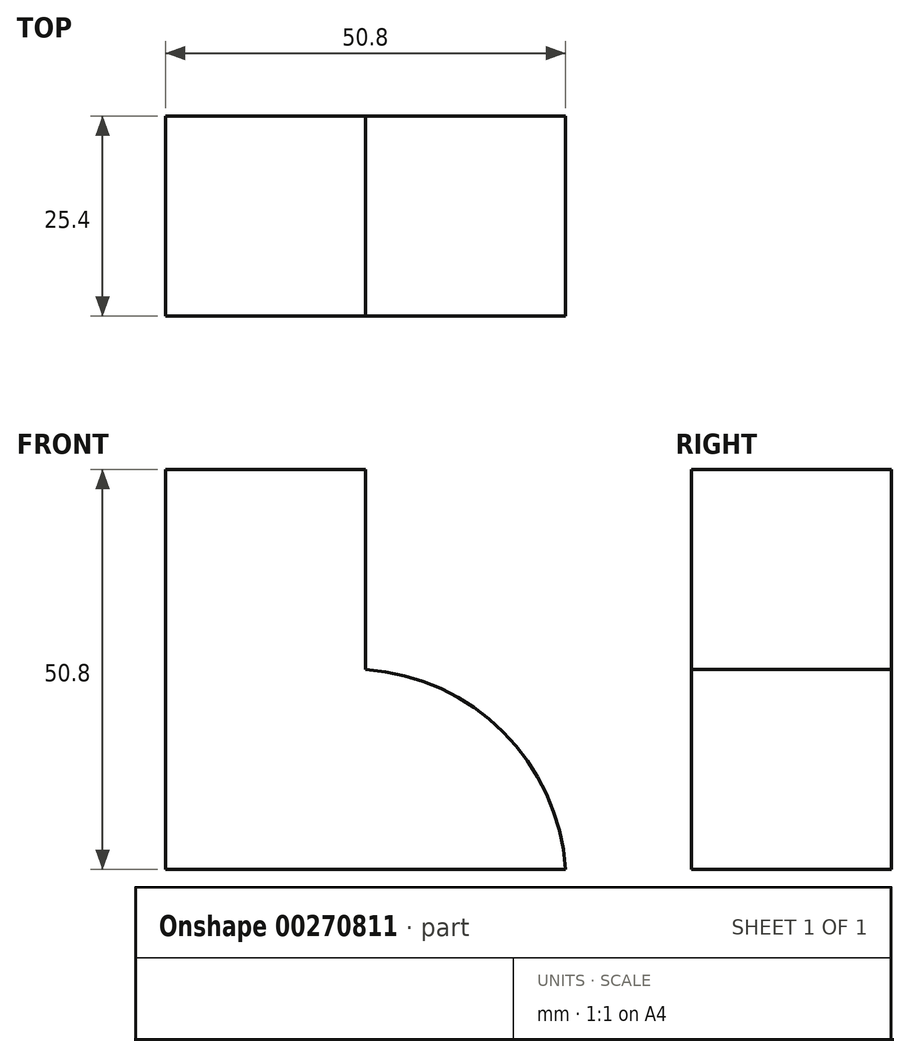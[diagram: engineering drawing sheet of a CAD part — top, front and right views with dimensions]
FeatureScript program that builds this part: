
annotation { "Feature Type Name" : "Feature", "Feature Type Description" : "" }
export const myFeature = defineFeature(function(context is Context, id is Id, definition is map)
    precondition{}
    {
        {
            var Q0;
            Q0=qCreatedBy(makeId("Front.planeOp"),FACE);
            var sketch = newSketch(context, id + "F0", { "sketchPlane" : qUnion([Q0])});
            skLineSegment(sketch, "E0", {"start": v(0, 0) * mm, "end": v(-50.8, 0) * mm});
            skLineSegment(sketch, "E1", {"start": v(-50.8, 0) * mm, "end": v(-50.8, 50.8) * mm});
            skLineSegment(sketch, "E2", {"start": v(-50.8, 50.8) * mm, "end": v(-25.4, 50.8) * mm});
            skLineSegment(sketch, "E3", {"start": v(-25.4, 50.8) * mm, "end": v(-25.4, 25.4) * mm});
            skArc(sketch, "E4", {"start": v(0, 0) * mm, "mid": v(-7.92, 17.48) * mm, "end": v(-25.4, 25.4) * mm});
            skSolve(sketch);
        }
        {
            var Q0;
            Q0=makeQuery(id+"F0.imprint","IMPRINT",FACE,{"disambiguationData":[TD([[makeQuery(id+"F0.imprint","IMPRINT",EDGE,{"derivedFrom":sQuery(id+"F0.wireOp",EDGE,"E0")}),-1.0]])]});
            extrude(context, id + "F1", {"entities" : qUnion([Q0]), "depth" : 25.4 * mm});
        }
    });
